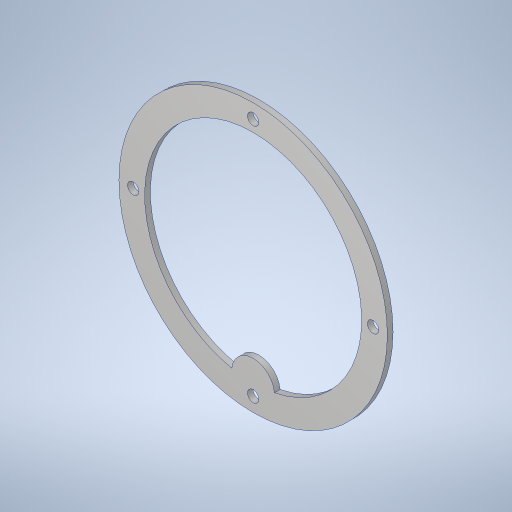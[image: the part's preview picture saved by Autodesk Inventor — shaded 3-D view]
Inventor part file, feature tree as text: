
AUTODESK INVENTOR PART (.ipt)
format: ipt  version: 2023.4 (Build 274418000, 418)  size: 263,680 bytes
history: native  units: in
note: dims shown in document units (in); Inventor stores cm internally (conversion verified against a paired STEP export)
features: extrude x1, sketch x1
ambient origin geometry x8: Origin, YZ Plane, XZ Plane, XY Plane, X Axis, Y Axis, Z Axis, Center Point
bodies: Solid1 (feature_tree)
feature tree (2):
  extrude  "Extrusion1"  Depth=0.1in
  sketch  "Sketch1"  dims[d0=3.8in d1=4.7in d2=0.75in d3=0.201in d4=0.25in d5=2.1in d6=1.5748in d8=360.0deg d10=0.1in d11=0.0in]
